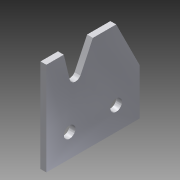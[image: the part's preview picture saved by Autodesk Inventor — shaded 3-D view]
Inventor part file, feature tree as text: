
AUTODESK INVENTOR PART (.ipt)
format: ipt  version: 2015 SP1 (Build 190203100, 203)  size: 115,712 bytes
history: native  units: in
note: dims shown in document units (in); Inventor stores cm internally (conversion verified against a paired STEP export)
features: sketch x2, extrude x1, hole x1
ambient origin geometry x8: Origin, YZ Plane, XZ Plane, XY Plane, X Axis, Y Axis, Z Axis, Center Point
bodies: Solid1 (feature_tree)
feature tree (4):
  extrude  "Extrusion1"  Depth=2.0in
  hole  "Hole1"  [1 undecoded]
  sketch  "Sketch1"  dims[d0=2.0in d1=2.0in]
  sketch  "Sketch2"  dims[d2=0.375in d3=0.5in d6=0.25in d7=0.5in d8=0.625in d9=0.125in d10=0.0in d11=0.5in d12=0.5in d13=0.5in d14=1.5in d15=0.25in d16=0.75in d17=0.375in d18=0.25in d19=0.5635in d20=1.0in d21=0.8108in d22=1.0in d23=0.5in]
note: 1 required parameter value undecoded (feature->parameter linkage not recoverable at this tier; creation-order binding heuristic only, values carry confidence <= 0.55)
